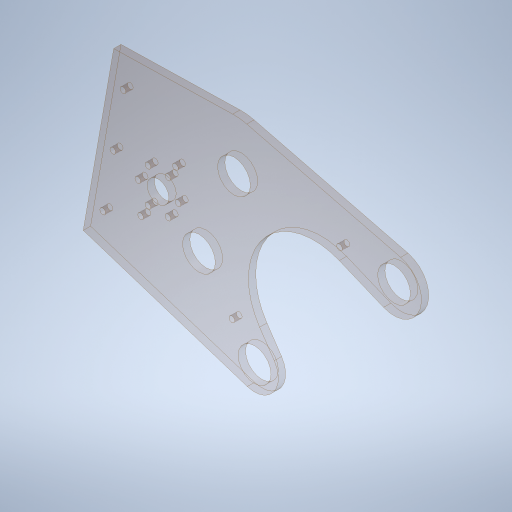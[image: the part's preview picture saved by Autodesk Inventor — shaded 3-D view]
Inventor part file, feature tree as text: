
AUTODESK INVENTOR PART (.ipt)
format: ipt  version: 2023.4 (Build 274418000, 418)  size: 351,744 bytes
history: native  units: in
note: dims shown in document units (in); Inventor stores cm internally (conversion verified against a paired STEP export)
features: sketch x1, extrude x1, hole x1
ambient origin geometry x8: Origin, YZ Plane, XZ Plane, XY Plane, X Axis, Y Axis, Z Axis, Center Point
bodies: Solid1 (feature_tree)
feature tree (3):
  sketch  "Sketch1"  dims[d3=45.0deg d4=0.0in d7=2.0in d8=4.25in d9=1.125in d10=3.0in d11=4.5in d12=4.5in d13=0.25in d14=0.375in d15=5.499in d16=1.128in d17=3.028in d18=3.126in d19=3.126in d22=1.0in d23=6.0in d26=8.0293in d27=2.0in d28=0.4688in d29=0.3504in d30=6.75in d31=0.0687in d32=0.75in d33=4.0in d34=1.375in d35=0.75in d36=0.25in d37=1.125in d38=2.3622in d40=360.0deg d43=0.1374in d44=0.375in d45=0.25in d46=0.0in d47=0.201in d48=0.75in d49=0.37in d50=0.25in d51=90.0deg d52=1.0in d53=0.8108in d55=0.5497in d56=0.3in]
  extrude  "Extrusion1"  TaperAngle=0.0deg  [1 undecoded]
  hole  "Hole1"  [1 undecoded]
note: 2 required parameter values undecoded (feature->parameter linkage not recoverable at this tier; creation-order binding heuristic only, values carry confidence <= 0.55)
